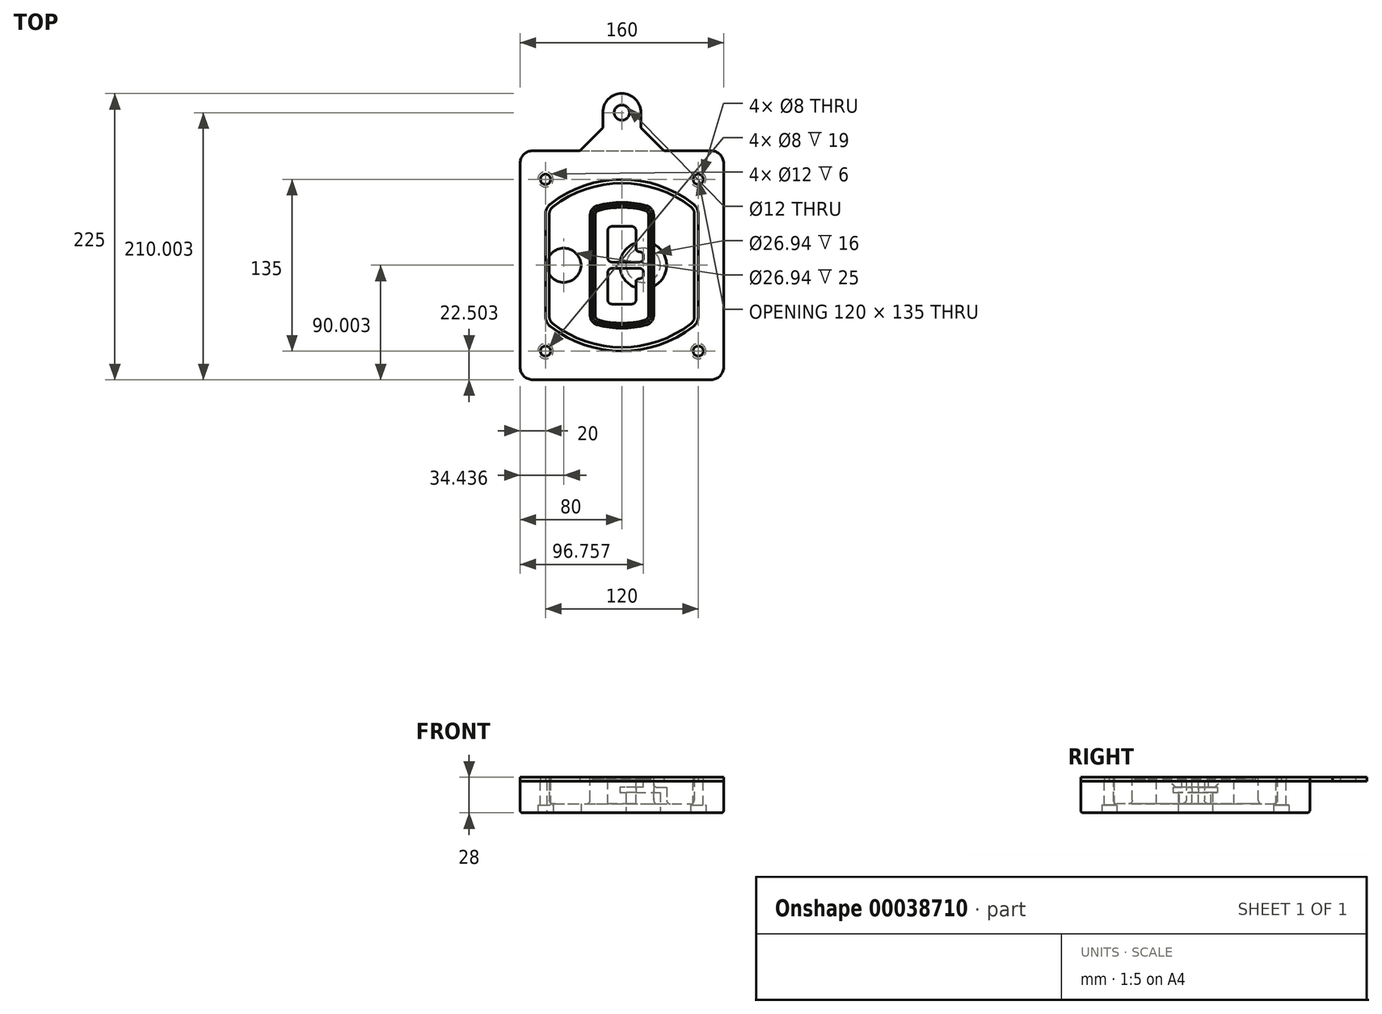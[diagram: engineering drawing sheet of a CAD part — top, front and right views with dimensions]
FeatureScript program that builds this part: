
annotation { "Feature Type Name" : "Feature", "Feature Type Description" : "" }
export const myFeature = defineFeature(function(context is Context, id is Id, definition is map)
    precondition{}
    {
        {
            var Q0;
            Q0=qCreatedBy(makeId("Top.planeOp"),FACE);
            var sketch = newSketch(context, id + "F0", { "sketchPlane" : qUnion([Q0])});
            skPoint(sketch, "E0.rect.middle", {"position": v(0, 0) * mm});
            skLineSegment(sketch, "E1.bottom", {"start": v(24.05, 28.38) * mm, "end": v(164.05, 28.38) * mm});
            skLineSegment(sketch, "E1.top", {"start": v(24.05, 208.38) * mm, "end": v(164.05, 208.38) * mm});
            skLineSegment(sketch, "E1.left", {"start": v(14.05, 38.38) * mm, "end": v(14.05, 198.38) * mm});
            skLineSegment(sketch, "E1.right", {"start": v(174.05, 38.38) * mm, "end": v(174.05, 198.38) * mm});
            skLineSegment(sketch, "E2", {"start": v(14.05, 208.38) * mm, "end": v(174.05, 28.38) * mm, "construction": true});
            skLineSegment(sketch, "E3", {"start": v(174.05, 208.38) * mm, "end": v(14.05, 28.38) * mm, "construction": true});
            skCircle(sketch, "E4", {"center": v(34.05, 185.88) * mm, "radius": 4 * mm});
            skCircle(sketch, "E5", {"center": v(154.05, 185.88) * mm, "radius": 4 * mm});
            skCircle(sketch, "E6", {"center": v(154.05, 50.88) * mm, "radius": 4 * mm});
            skCircle(sketch, "E7", {"center": v(34.05, 50.88) * mm, "radius": 4 * mm});
            skLineSegment(sketch, "E8", {"start": v(34.05, 185.88) * mm, "end": v(154.05, 185.88) * mm, "construction": true});
            skLineSegment(sketch, "E9", {"start": v(154.05, 185.88) * mm, "end": v(154.05, 50.88) * mm, "construction": true});
            skLineSegment(sketch, "E10", {"start": v(154.05, 50.88) * mm, "end": v(34.05, 50.88) * mm, "construction": true});
            skLineSegment(sketch, "E11", {"start": v(34.05, 50.88) * mm, "end": v(34.05, 185.88) * mm, "construction": true});
            skLineSegment(sketch, "E12", {"start": v(34.05, 158.68) * mm, "end": v(34.05, 78.09) * mm});
            skLineSegment(sketch, "E13", {"start": v(154.05, 158.68) * mm, "end": v(154.05, 78.09) * mm});
            skArc(sketch, "E14", {"start": v(150.2, 166.56) * mm, "mid": v(94.05, 185.88) * mm, "end": v(37.9, 166.56) * mm});
            skArc(sketch, "E15", {"start": v(37.9, 70.2) * mm, "mid": v(94.05, 50.88) * mm, "end": v(150.2, 70.2) * mm});
            skLineSegment(sketch, "E16", {"start": v(34.05, 118.38) * mm, "end": v(154.05, 118.38) * mm, "construction": true});
            skPoint(sketch, "E17.visualSharp", {"position": v(34.05, 73.38) * mm});
            skArc(sketch, "E17.filletArc", {"start": v(34.05, 78.09) * mm, "mid": v(35.06, 73.7) * mm, "end": v(37.9, 70.2) * mm});
            skPoint(sketch, "E18.visualSharp", {"position": v(34.05, 163.38) * mm});
            skArc(sketch, "E18.filletArc", {"start": v(37.9, 166.56) * mm, "mid": v(35.06, 163.06) * mm, "end": v(34.05, 158.68) * mm});
            skPoint(sketch, "E19.visualSharp", {"position": v(154.05, 163.38) * mm});
            skArc(sketch, "E19.filletArc", {"start": v(154.05, 158.68) * mm, "mid": v(153.04, 163.06) * mm, "end": v(150.2, 166.56) * mm});
            skPoint(sketch, "E20.visualSharp", {"position": v(154.05, 73.38) * mm});
            skArc(sketch, "E20.filletArc", {"start": v(150.2, 70.2) * mm, "mid": v(153.04, 73.7) * mm, "end": v(154.05, 78.09) * mm});
            skPoint(sketch, "E21.visualSharp", {"position": v(14.05, 208.38) * mm});
            skArc(sketch, "E21.filletArc", {"start": v(24.05, 208.38) * mm, "mid": v(16.98, 205.45) * mm, "end": v(14.05, 198.38) * mm});
            skPoint(sketch, "E22.visualSharp", {"position": v(174.05, 208.38) * mm});
            skArc(sketch, "E22.filletArc", {"start": v(174.05, 198.38) * mm, "mid": v(171.12, 205.45) * mm, "end": v(164.05, 208.38) * mm});
            skPoint(sketch, "E23.visualSharp", {"position": v(174.05, 28.38) * mm});
            skArc(sketch, "E23.filletArc", {"start": v(164.05, 28.38) * mm, "mid": v(171.12, 31.31) * mm, "end": v(174.05, 38.38) * mm});
            skPoint(sketch, "E24.visualSharp", {"position": v(14.05, 28.38) * mm});
            skArc(sketch, "E24.filletArc", {"start": v(14.05, 38.38) * mm, "mid": v(16.98, 31.31) * mm, "end": v(24.05, 28.38) * mm});
            skArc(sketch, "E25.0", {"start": v(151.05, 158.68) * mm, "mid": v(150.34, 161.75) * mm, "end": v(148.36, 164.2) * mm});
            skLineSegment(sketch, "E25.1", {"start": v(151.05, 158.68) * mm, "end": v(151.05, 78.09) * mm});
            skArc(sketch, "E25.2", {"start": v(148.36, 72.57) * mm, "mid": v(150.34, 75.02) * mm, "end": v(151.05, 78.09) * mm});
            skArc(sketch, "E25.3", {"start": v(39.74, 72.57) * mm, "mid": v(94.05, 53.88) * mm, "end": v(148.36, 72.57) * mm});
            skArc(sketch, "E25.4", {"start": v(37.05, 78.09) * mm, "mid": v(37.76, 75.02) * mm, "end": v(39.74, 72.57) * mm});
            skArc(sketch, "E25.5", {"start": v(148.36, 164.2) * mm, "mid": v(94.05, 182.88) * mm, "end": v(39.74, 164.2) * mm});
            skLineSegment(sketch, "E25.6", {"start": v(37.05, 158.68) * mm, "end": v(37.05, 78.09) * mm});
            skArc(sketch, "E25.7", {"start": v(39.74, 164.2) * mm, "mid": v(37.76, 161.75) * mm, "end": v(37.05, 158.68) * mm});
            skArc(sketch, "E26.0", {"start": v(35.43, 169.71) * mm, "mid": v(31.47, 164.82) * mm, "end": v(30.05, 158.68) * mm});
            skArc(sketch, "E26.1", {"start": v(152.67, 169.71) * mm, "mid": v(94.05, 189.88) * mm, "end": v(35.43, 169.71) * mm});
            skArc(sketch, "E26.2", {"start": v(158.05, 158.68) * mm, "mid": v(156.63, 164.82) * mm, "end": v(152.67, 169.71) * mm});
            skLineSegment(sketch, "E26.3", {"start": v(158.05, 158.68) * mm, "end": v(158.05, 78.09) * mm});
            skArc(sketch, "E26.4", {"start": v(152.67, 67.05) * mm, "mid": v(156.63, 71.95) * mm, "end": v(158.05, 78.09) * mm});
            skLineSegment(sketch, "E26.5", {"start": v(30.05, 158.68) * mm, "end": v(30.05, 78.09) * mm});
            skArc(sketch, "E26.6", {"start": v(35.43, 67.05) * mm, "mid": v(94.05, 46.88) * mm, "end": v(152.67, 67.05) * mm});
            skArc(sketch, "E26.7", {"start": v(30.05, 78.09) * mm, "mid": v(31.47, 71.95) * mm, "end": v(35.43, 67.05) * mm});
            skSolve(sketch);
        }
        {
            var Q0;
            Q0=makeQuery(id+"F0.imprint","IMPRINT",FACE,{"disambiguationData":[TD([[makeQuery(id+"F0.imprint","IMPRINT",EDGE,{"derivedFrom":sQuery(id+"F0.wireOp",EDGE,"E1.bottom")}),1.0]])]});
            var Q1;
            Q1=makeQuery(id+"F0.imprint","IMPRINT",FACE,{"disambiguationData":[TD([[makeQuery(id+"F0.imprint","IMPRINT",EDGE,{"derivedFrom":sQuery(id+"F0.wireOp",EDGE,"E12")}),1.0]])]});
            var Q2;
            Q2=makeQuery(id+"F0.imprint","IMPRINT",FACE,{"disambiguationData":[TD([[makeQuery(id+"F0.imprint","IMPRINT",EDGE,{"derivedFrom":sQuery(id+"F0.wireOp",EDGE,"E25.0")}),1.0]])]});
            var Q3;
            Q3=makeQuery(id+"F0.imprint","IMPRINT",FACE,{"disambiguationData":[TD([[makeQuery(id+"F0.imprint","IMPRINT",EDGE,{"derivedFrom":sQuery(id+"F0.wireOp",EDGE,"E12")}),-1.0]])]});
            extrude(context, id + "F1", {"entities" : qUnion([Q0, Q1, Q2, Q3]), "oppositeDirection" : true, "depth" : 25 * mm});
        }
        {
            var Q0;
            Q0=makeQuery(id+"F0.imprint","IMPRINT",FACE,{"disambiguationData":[TD([[makeQuery(id+"F0.imprint","IMPRINT",EDGE,{"derivedFrom":sQuery(id+"F0.wireOp",EDGE,"E12")}),1.0]])]});
            extrude(context, id + "F2", {"entities" : qUnion([Q0]), "operationType" : NewBodyOperationType.ADD, "depth" : 3 * mm});
        }
        {
            var Q0;
            Q0=makeQuery(id+"F0.imprint","IMPRINT",FACE,{"disambiguationData":[TD([[makeQuery(id+"F0.imprint","IMPRINT",EDGE,{"derivedFrom":sQuery(id+"F0.wireOp",EDGE,"E25.0")}),1.0]])]});
            extrude(context, id + "F3", {"entities" : qUnion([Q0]), "operationType" : NewBodyOperationType.REMOVE, "oppositeDirection" : true, "depth" : 18 * mm});
        }
        {
            var Q0;
            Q0=makeQuery(id+"F2.opExtrude","CAP_FACE",FACE,{"disambiguationData":[OSD([sQuery(id+"F0.wireOp",EDGE,"E12"),sQuery(id+"F0.wireOp",EDGE,"E13"),sQuery(id+"F0.wireOp",EDGE,"E14"),sQuery(id+"F0.wireOp",EDGE,"E15"),sQuery(id+"F0.wireOp",EDGE,"E17.filletArc"),sQuery(id+"F0.wireOp",EDGE,"E18.filletArc"),sQuery(id+"F0.wireOp",EDGE,"E19.filletArc"),sQuery(id+"F0.wireOp",EDGE,"E20.filletArc"),sQuery(id+"F0.wireOp",EDGE,"E25.0"),sQuery(id+"F0.wireOp",EDGE,"E25.1"),sQuery(id+"F0.wireOp",EDGE,"E25.2"),sQuery(id+"F0.wireOp",EDGE,"E25.3"),sQuery(id+"F0.wireOp",EDGE,"E25.4"),sQuery(id+"F0.wireOp",EDGE,"E25.5"),sQuery(id+"F0.wireOp",EDGE,"E25.6"),sQuery(id+"F0.wireOp",EDGE,"E25.7")])],"isStart":false});
            var sketch = newSketch(context, id + "F4", { "sketchPlane" : qUnion([Q0])});
            skArc(sketch, "E27.0", {"start": v(74.97, 71.41) * mm, "mid": v(94.05, 68.88) * mm, "end": v(113.13, 71.41) * mm});
            skArc(sketch, "E28.0", {"start": v(113.13, 165.35) * mm, "mid": v(94.05, 167.88) * mm, "end": v(74.97, 165.35) * mm});
            skLineSegment(sketch, "E29", {"start": v(69.05, 157.63) * mm, "end": v(69.05, 79.14) * mm});
            skLineSegment(sketch, "E30", {"start": v(119.05, 157.63) * mm, "end": v(119.05, 79.14) * mm});
            skLineSegment(sketch, "E31", {"start": v(69.05, 163.48) * mm, "end": v(119.05, 163.48) * mm, "construction": true});
            skLineSegment(sketch, "E32", {"start": v(69.05, 73.28) * mm, "end": v(119.05, 73.28) * mm, "construction": true});
            skPoint(sketch, "E33.visualSharp", {"position": v(69.05, 163.48) * mm});
            skArc(sketch, "E33.filletArc", {"start": v(74.97, 165.35) * mm, "mid": v(70.7, 162.5) * mm, "end": v(69.05, 157.63) * mm});
            skPoint(sketch, "E34.visualSharp", {"position": v(119.05, 163.48) * mm});
            skArc(sketch, "E34.filletArc", {"start": v(119.05, 157.63) * mm, "mid": v(117.4, 162.5) * mm, "end": v(113.13, 165.35) * mm});
            skPoint(sketch, "E35.visualSharp", {"position": v(119.05, 73.28) * mm});
            skArc(sketch, "E35.filletArc", {"start": v(113.13, 71.41) * mm, "mid": v(117.4, 74.27) * mm, "end": v(119.05, 79.14) * mm});
            skPoint(sketch, "E36.visualSharp", {"position": v(69.05, 73.28) * mm});
            skArc(sketch, "E36.filletArc", {"start": v(69.05, 79.14) * mm, "mid": v(70.7, 74.27) * mm, "end": v(74.97, 71.41) * mm});
            skArc(sketch, "E37.0", {"start": v(148.36, 164.2) * mm, "mid": v(94.05, 182.88) * mm, "end": v(39.74, 164.2) * mm});
            skArc(sketch, "E37.1", {"start": v(39.74, 164.2) * mm, "mid": v(37.76, 161.75) * mm, "end": v(37.05, 158.68) * mm});
            skLineSegment(sketch, "E37.2", {"start": v(37.05, 158.68) * mm, "end": v(37.05, 78.09) * mm});
            skArc(sketch, "E37.3", {"start": v(37.05, 78.09) * mm, "mid": v(37.76, 75.02) * mm, "end": v(39.74, 72.57) * mm});
            skArc(sketch, "E37.4", {"start": v(39.74, 72.57) * mm, "mid": v(94.05, 53.88) * mm, "end": v(148.36, 72.57) * mm});
            skArc(sketch, "E37.5", {"start": v(148.36, 72.57) * mm, "mid": v(150.34, 75.02) * mm, "end": v(151.05, 78.09) * mm});
            skLineSegment(sketch, "E37.6", {"start": v(151.05, 158.68) * mm, "end": v(151.05, 78.09) * mm});
            skArc(sketch, "E37.7", {"start": v(151.05, 158.68) * mm, "mid": v(150.34, 161.75) * mm, "end": v(148.36, 164.2) * mm});
            skLineSegment(sketch, "E38.0", {"start": v(117.05, 157.63) * mm, "end": v(117.05, 79.14) * mm});
            skArc(sketch, "E38.1", {"start": v(112.61, 73.34) * mm, "mid": v(115.81, 75.49) * mm, "end": v(117.05, 79.14) * mm});
            skArc(sketch, "E38.2", {"start": v(75.49, 73.34) * mm, "mid": v(94.05, 70.88) * mm, "end": v(112.61, 73.34) * mm});
            skArc(sketch, "E38.3", {"start": v(71.05, 79.14) * mm, "mid": v(72.29, 75.49) * mm, "end": v(75.49, 73.34) * mm});
            skLineSegment(sketch, "E38.4", {"start": v(71.05, 157.63) * mm, "end": v(71.05, 79.14) * mm});
            skArc(sketch, "E38.5", {"start": v(117.05, 157.63) * mm, "mid": v(115.81, 161.28) * mm, "end": v(112.61, 163.42) * mm});
            skArc(sketch, "E38.6", {"start": v(75.49, 163.42) * mm, "mid": v(72.29, 161.28) * mm, "end": v(71.05, 157.63) * mm});
            skArc(sketch, "E38.7", {"start": v(112.61, 163.42) * mm, "mid": v(94.05, 165.88) * mm, "end": v(75.49, 163.42) * mm});
            skArc(sketch, "E39.0", {"start": v(115.05, 157.63) * mm, "mid": v(114.23, 160.06) * mm, "end": v(112.1, 161.5) * mm});
            skLineSegment(sketch, "E39.1", {"start": v(115.05, 157.63) * mm, "end": v(115.05, 79.14) * mm});
            skArc(sketch, "E39.2", {"start": v(112.1, 75.27) * mm, "mid": v(114.23, 76.7) * mm, "end": v(115.05, 79.14) * mm});
            skArc(sketch, "E39.3", {"start": v(76, 75.27) * mm, "mid": v(94.05, 72.88) * mm, "end": v(112.1, 75.27) * mm});
            skArc(sketch, "E39.4", {"start": v(73.05, 79.14) * mm, "mid": v(73.87, 76.7) * mm, "end": v(76, 75.27) * mm});
            skArc(sketch, "E39.5", {"start": v(112.1, 161.5) * mm, "mid": v(94.05, 163.88) * mm, "end": v(76, 161.5) * mm});
            skLineSegment(sketch, "E39.6", {"start": v(73.05, 157.63) * mm, "end": v(73.05, 79.14) * mm});
            skArc(sketch, "E39.7", {"start": v(76, 161.5) * mm, "mid": v(73.87, 160.06) * mm, "end": v(73.05, 157.63) * mm});
            skLineSegment(sketch, "E40", {"start": v(69.05, 118.38) * mm, "end": v(119.05, 118.38) * mm, "construction": true});
            skLineSegment(sketch, "E41", {"start": v(83.05, 123.88) * mm, "end": v(83.05, 145.88) * mm});
            skLineSegment(sketch, "E42", {"start": v(86.05, 148.88) * mm, "end": v(102.05, 148.88) * mm});
            skLineSegment(sketch, "E43", {"start": v(105.05, 145.88) * mm, "end": v(105.05, 131.88) * mm});
            skLineSegment(sketch, "E44", {"start": v(108.05, 128.88) * mm, "end": v(108.05, 128.88) * mm});
            skLineSegment(sketch, "E45", {"start": v(111.05, 125.88) * mm, "end": v(111.05, 123.88) * mm});
            skLineSegment(sketch, "E46", {"start": v(108.05, 120.88) * mm, "end": v(86.05, 120.88) * mm});
            skPoint(sketch, "E47.visualSharp", {"position": v(83.05, 148.88) * mm});
            skArc(sketch, "E47.filletArc", {"start": v(86.05, 148.88) * mm, "mid": v(83.93, 148) * mm, "end": v(83.05, 145.88) * mm});
            skPoint(sketch, "E48.visualSharp", {"position": v(105.05, 148.88) * mm});
            skArc(sketch, "E48.filletArc", {"start": v(105.05, 145.88) * mm, "mid": v(104.17, 148) * mm, "end": v(102.05, 148.88) * mm});
            skPoint(sketch, "E49.visualSharp", {"position": v(105.05, 128.88) * mm});
            skArc(sketch, "E49.filletArc", {"start": v(105.05, 131.88) * mm, "mid": v(105.93, 129.76) * mm, "end": v(108.05, 128.88) * mm});
            skPoint(sketch, "E50.visualSharp", {"position": v(111.05, 128.88) * mm});
            skArc(sketch, "E50.filletArc", {"start": v(111.05, 125.88) * mm, "mid": v(110.17, 128) * mm, "end": v(108.05, 128.88) * mm});
            skPoint(sketch, "E51.visualSharp", {"position": v(111.05, 120.88) * mm});
            skArc(sketch, "E51.filletArc", {"start": v(108.05, 120.88) * mm, "mid": v(110.17, 121.76) * mm, "end": v(111.05, 123.88) * mm});
            skPoint(sketch, "E52.visualSharp", {"position": v(83.05, 120.88) * mm});
            skArc(sketch, "E52.filletArc", {"start": v(83.05, 123.88) * mm, "mid": v(83.93, 121.76) * mm, "end": v(86.05, 120.88) * mm});
            skLineSegment(sketch, "E53.0.MirrorCS", {"start": v(108.05, 115.88) * mm, "end": v(86.05, 115.88) * mm});
            skArc(sketch, "E54.0.MirrorCS", {"start": v(83.05, 112.88) * mm, "mid": v(83.93, 115) * mm, "end": v(86.05, 115.88) * mm});
            skLineSegment(sketch, "E55.0.MirrorCS", {"start": v(83.05, 112.88) * mm, "end": v(83.05, 90.88) * mm});
            skArc(sketch, "E56.0.MirrorCS", {"start": v(86.05, 87.88) * mm, "mid": v(83.93, 88.76) * mm, "end": v(83.05, 90.88) * mm});
            skLineSegment(sketch, "E57.0.MirrorCS", {"start": v(86.05, 87.88) * mm, "end": v(102.05, 87.88) * mm});
            skArc(sketch, "E58.0.MirrorCS", {"start": v(105.05, 90.88) * mm, "mid": v(104.17, 88.76) * mm, "end": v(102.05, 87.88) * mm});
            skLineSegment(sketch, "E59.0.MirrorCS", {"start": v(105.05, 90.88) * mm, "end": v(105.05, 104.88) * mm});
            skArc(sketch, "E60.0.MirrorCS", {"start": v(105.05, 104.88) * mm, "mid": v(105.93, 107) * mm, "end": v(108.05, 107.88) * mm});
            skArc(sketch, "E61.0.MirrorCS", {"start": v(111.05, 110.88) * mm, "mid": v(110.17, 108.76) * mm, "end": v(108.05, 107.88) * mm});
            skLineSegment(sketch, "E62.0.MirrorCS", {"start": v(111.05, 110.88) * mm, "end": v(111.05, 112.88) * mm});
            skArc(sketch, "E63.0.MirrorCS", {"start": v(108.05, 115.88) * mm, "mid": v(110.17, 115) * mm, "end": v(111.05, 112.88) * mm});
            skSolve(sketch);
        }
        {
            var Q0;
            Q0=makeQuery(id+"F4.imprint","IMPRINT",FACE,{"disambiguationData":[TD([[makeQuery(id+"F4.imprint","IMPRINT",EDGE,{"derivedFrom":sQuery(id+"F4.wireOp",EDGE,"E27.0")}),1.0]])]});
            var Q1;
            Q1=makeQuery(id+"F4.imprint","IMPRINT",FACE,{"disambiguationData":[TD([[makeQuery(id+"F4.imprint","IMPRINT",EDGE,{"derivedFrom":sQuery(id+"F4.wireOp",EDGE,"E38.0")}),-1.0]])]});
            var Q2;
            Q2=makeQuery(id+"F4.imprint","IMPRINT",FACE,{"disambiguationData":[TD([[makeQuery(id+"F4.imprint","IMPRINT",EDGE,{"derivedFrom":sQuery(id+"F4.wireOp",EDGE,"E39.0")}),1.0]])]});
            extrude(context, id + "F5", {"entities" : qUnion([Q0, Q1, Q2]), "operationType" : NewBodyOperationType.ADD, "endBound" : BoundingType.UP_TO_NEXT, "oppositeDirection" : true, "depth" : 25 * mm});
        }
        {
            var Q0;
            Q0=makeQuery(id+"F4.imprint","IMPRINT",FACE,{"disambiguationData":[TD([[makeQuery(id+"F4.imprint","IMPRINT",EDGE,{"derivedFrom":sQuery(id+"F4.wireOp",EDGE,"E38.0")}),-1.0]])]});
            extrude(context, id + "F6", {"entities" : qUnion([Q0]), "operationType" : NewBodyOperationType.REMOVE, "oppositeDirection" : true, "depth" : 2 * mm});
        }
        {
            var Q0;
            Q0=makeQuery(id+"F1.opExtrude","CAP_FACE",FACE,{"disambiguationData":[OSD([sQuery(id+"F0.wireOp",EDGE,"E1.bottom"),sQuery(id+"F0.wireOp",EDGE,"E1.top"),sQuery(id+"F0.wireOp",EDGE,"E1.left"),sQuery(id+"F0.wireOp",EDGE,"E1.right"),sQuery(id+"F0.wireOp",EDGE,"E4"),sQuery(id+"F0.wireOp",EDGE,"E5"),sQuery(id+"F0.wireOp",EDGE,"E6"),sQuery(id+"F0.wireOp",EDGE,"E7"),sQuery(id+"F0.wireOp",EDGE,"E21.filletArc"),sQuery(id+"F0.wireOp",EDGE,"E22.filletArc"),sQuery(id+"F0.wireOp",EDGE,"E23.filletArc"),sQuery(id+"F0.wireOp",EDGE,"E24.filletArc")])],"isStart":false});
            var sketch = newSketch(context, id + "F7", { "sketchPlane" : qUnion([Q0])});
            skCircle(sketch, "E64", {"center": v(110.8, -118.38) * mm, "radius": 13.47 * mm});
            skCircle(sketch, "E65", {"center": v(48.49, -118.38) * mm, "radius": 13.47 * mm});
            skLineSegment(sketch, "E66", {"start": v(174.05, -118.38) * mm, "end": v(14.05, -118.38) * mm});
            skCircle(sketch, "E67", {"center": v(110.8, -118.38) * mm, "radius": 18.47 * mm});
            skCircle(sketch, "E68", {"center": v(154.05, -185.88) * mm, "radius": 6 * mm});
            skCircle(sketch, "E69", {"center": v(34.05, -185.88) * mm, "radius": 6 * mm});
            skCircle(sketch, "E70", {"center": v(34.05, -50.88) * mm, "radius": 6 * mm});
            skCircle(sketch, "E71", {"center": v(154.05, -50.88) * mm, "radius": 6 * mm});
            skSolve(sketch);
        }
        {
            var Q0;
            {var subQ1=sQuery(id+"F7.wireOp",EDGE,"E66");var subQ4=sQuery(id+"F7.wireOp",EDGE,"E64");var subQ6=makeQuery(id+"F7.imprint","INTERSECT",VERTEX,{"disambiguationData":[OD(0.0)],"derivedFrom":[subQ4,subQ1]});Q0=makeQuery(id+"F7.imprint","IMPRINT",FACE,{"disambiguationData":[TD([[makeQuery(id+"F7.imprint","IMPRINT",EDGE,{"disambiguationData":[TD([[subQ6,-1.0]])],"derivedFrom":subQ4}),-1.0]])]});}
            var Q1;
            {var subQ0=sQuery(id+"F7.wireOp",EDGE,"E66");var subQ1=sQuery(id+"F7.wireOp",EDGE,"E64");var subQ3=makeQuery(id+"F7.imprint","INTERSECT",VERTEX,{"disambiguationData":[OD(0.0)],"derivedFrom":[subQ1,subQ0]});Q1=makeQuery(id+"F7.imprint","IMPRINT",FACE,{"disambiguationData":[TD([[makeQuery(id+"F7.imprint","IMPRINT",EDGE,{"disambiguationData":[TD([[subQ3,-1.0]])],"derivedFrom":subQ1}),1.0]])]});}
            var Q2;
            {var subQ0=sQuery(id+"F7.wireOp",EDGE,"E66");var subQ1=sQuery(id+"F7.wireOp",EDGE,"E64");var subQ3=makeQuery(id+"F7.imprint","INTERSECT",VERTEX,{"disambiguationData":[OD(0.0)],"derivedFrom":[subQ1,subQ0]});Q2=makeQuery(id+"F7.imprint","IMPRINT",FACE,{"disambiguationData":[TD([[makeQuery(id+"F7.imprint","IMPRINT",EDGE,{"disambiguationData":[TD([[subQ3,1.0]])],"derivedFrom":subQ1}),1.0]])]});}
            var Q3;
            {var subQ1=sQuery(id+"F7.wireOp",EDGE,"E66");var subQ4=sQuery(id+"F7.wireOp",EDGE,"E64");var subQ6=makeQuery(id+"F7.imprint","INTERSECT",VERTEX,{"disambiguationData":[OD(0.0)],"derivedFrom":[subQ4,subQ1]});Q3=makeQuery(id+"F7.imprint","IMPRINT",FACE,{"disambiguationData":[TD([[makeQuery(id+"F7.imprint","IMPRINT",EDGE,{"disambiguationData":[TD([[subQ6,1.0]])],"derivedFrom":subQ4}),-1.0]])]});}
            extrude(context, id + "F8", {"entities" : qUnion([Q0, Q1, Q2, Q3]), "operationType" : NewBodyOperationType.ADD, "oppositeDirection" : true, "depth" : 20 * mm});
        }
        {
            var Q0;
            {var subQ0=sQuery(id+"F7.wireOp",EDGE,"E66");var subQ1=sQuery(id+"F7.wireOp",EDGE,"E64");var subQ3=makeQuery(id+"F7.imprint","INTERSECT",VERTEX,{"disambiguationData":[OD(0.0)],"derivedFrom":[subQ1,subQ0]});Q0=makeQuery(id+"F7.imprint","IMPRINT",FACE,{"disambiguationData":[TD([[makeQuery(id+"F7.imprint","IMPRINT",EDGE,{"disambiguationData":[TD([[subQ3,-1.0]])],"derivedFrom":subQ1}),1.0]])]});}
            var Q1;
            {var subQ0=sQuery(id+"F7.wireOp",EDGE,"E66");var subQ1=sQuery(id+"F7.wireOp",EDGE,"E64");var subQ3=makeQuery(id+"F7.imprint","INTERSECT",VERTEX,{"disambiguationData":[OD(0.0)],"derivedFrom":[subQ1,subQ0]});Q1=makeQuery(id+"F7.imprint","IMPRINT",FACE,{"disambiguationData":[TD([[makeQuery(id+"F7.imprint","IMPRINT",EDGE,{"disambiguationData":[TD([[subQ3,1.0]])],"derivedFrom":subQ1}),1.0]])]});}
            extrude(context, id + "F9", {"entities" : qUnion([Q0, Q1]), "operationType" : NewBodyOperationType.REMOVE, "oppositeDirection" : true, "depth" : 16 * mm});
        }
        {
            var Q0;
            {var subQ0=sQuery(id+"F7.wireOp",EDGE,"E66");var subQ1=sQuery(id+"F7.wireOp",EDGE,"E65");var subQ3=makeQuery(id+"F7.imprint","INTERSECT",VERTEX,{"disambiguationData":[OD(0.0)],"derivedFrom":[subQ1,subQ0]});Q0=makeQuery(id+"F7.imprint","IMPRINT",FACE,{"disambiguationData":[TD([[makeQuery(id+"F7.imprint","IMPRINT",EDGE,{"disambiguationData":[TD([[subQ3,-1.0]])],"derivedFrom":subQ1}),1.0]])]});}
            var Q1;
            {var subQ0=sQuery(id+"F7.wireOp",EDGE,"E66");var subQ1=sQuery(id+"F7.wireOp",EDGE,"E65");var subQ3=makeQuery(id+"F7.imprint","INTERSECT",VERTEX,{"disambiguationData":[OD(0.0)],"derivedFrom":[subQ1,subQ0]});Q1=makeQuery(id+"F7.imprint","IMPRINT",FACE,{"disambiguationData":[TD([[makeQuery(id+"F7.imprint","IMPRINT",EDGE,{"disambiguationData":[TD([[subQ3,1.0]])],"derivedFrom":subQ1}),1.0]])]});}
            extrude(context, id + "F10", {"entities" : qUnion([Q0, Q1]), "operationType" : NewBodyOperationType.REMOVE, "oppositeDirection" : true, "depth" : 25 * mm});
        }
        {
            var Q0;
            Q0=makeQuery(id+"F7.imprint","IMPRINT",FACE,{"disambiguationData":[TD([[makeQuery(id+"F7.imprint","IMPRINT",EDGE,{"derivedFrom":sQuery(id+"F7.wireOp",EDGE,"E68")}),1.0]])]});
            var Q1;
            Q1=makeQuery(id+"F7.imprint","IMPRINT",FACE,{"disambiguationData":[TD([[makeQuery(id+"F7.imprint","IMPRINT",EDGE,{"derivedFrom":makeQuery(id+"F1.opExtrude","CAP_EDGE",EDGE,{"disambiguationData":[OSD([sQuery(id+"F0.wireOp",EDGE,"E5")])],"isStart":false})}),-1.0]])]});
            var Q2;
            Q2=makeQuery(id+"F7.imprint","IMPRINT",FACE,{"disambiguationData":[TD([[makeQuery(id+"F7.imprint","IMPRINT",EDGE,{"derivedFrom":sQuery(id+"F7.wireOp",EDGE,"E69")}),1.0]])]});
            var Q3;
            Q3=makeQuery(id+"F7.imprint","IMPRINT",FACE,{"disambiguationData":[TD([[makeQuery(id+"F7.imprint","IMPRINT",EDGE,{"derivedFrom":makeQuery(id+"F1.opExtrude","CAP_EDGE",EDGE,{"disambiguationData":[OSD([sQuery(id+"F0.wireOp",EDGE,"E4")])],"isStart":false})}),-1.0]])]});
            var Q4;
            Q4=makeQuery(id+"F7.imprint","IMPRINT",FACE,{"disambiguationData":[TD([[makeQuery(id+"F7.imprint","IMPRINT",EDGE,{"derivedFrom":sQuery(id+"F7.wireOp",EDGE,"E70")}),1.0]])]});
            var Q5;
            Q5=makeQuery(id+"F7.imprint","IMPRINT",FACE,{"disambiguationData":[TD([[makeQuery(id+"F7.imprint","IMPRINT",EDGE,{"derivedFrom":makeQuery(id+"F1.opExtrude","CAP_EDGE",EDGE,{"disambiguationData":[OSD([sQuery(id+"F0.wireOp",EDGE,"E7")])],"isStart":false})}),-1.0]])]});
            var Q6;
            Q6=makeQuery(id+"F7.imprint","IMPRINT",FACE,{"disambiguationData":[TD([[makeQuery(id+"F7.imprint","IMPRINT",EDGE,{"derivedFrom":sQuery(id+"F7.wireOp",EDGE,"E71")}),1.0]])]});
            var Q7;
            Q7=makeQuery(id+"F7.imprint","IMPRINT",FACE,{"disambiguationData":[TD([[makeQuery(id+"F7.imprint","IMPRINT",EDGE,{"derivedFrom":makeQuery(id+"F1.opExtrude","CAP_EDGE",EDGE,{"disambiguationData":[OSD([sQuery(id+"F0.wireOp",EDGE,"E6")])],"isStart":false})}),-1.0]])]});
            extrude(context, id + "F11", {"entities" : qUnion([Q0, Q1, Q2, Q3, Q4, Q5, Q6, Q7]), "operationType" : NewBodyOperationType.REMOVE, "oppositeDirection" : true, "depth" : 6 * mm});
        }
        {
            var Q0;
            Q0=makeQuery(id+"F9.boolean.opBoolean","COPY",FACE,{"derivedFrom":makeQuery(id+"F9.opExtrude","CAP_FACE",FACE,{"disambiguationData":[OSD([sQuery(id+"F7.wireOp",EDGE,"E64")])],"isStart":false})});
            var sketch = newSketch(context, id + "F12", { "sketchPlane" : qUnion([Q0])});
            skArc(sketch, "E72.0", {"start": v(105.05, -100.83) * mm, "mid": v(96.62, -106.56) * mm, "end": v(92.5, -115.88) * mm});
            skArc(sketch, "E72.1", {"start": v(92.5, -120.88) * mm, "mid": v(96.62, -130.2) * mm, "end": v(105.05, -135.93) * mm});
            skLineSegment(sketch, "E73", {"start": v(92.5, -120.88) * mm, "end": v(108.05, -120.88) * mm});
            skLineSegment(sketch, "E74.0", {"start": v(108.05, -115.88) * mm, "end": v(92.5, -115.88) * mm});
            skArc(sketch, "E74.1", {"start": v(108.05, -115.88) * mm, "mid": v(110.17, -115) * mm, "end": v(111.05, -112.88) * mm});
            skLineSegment(sketch, "E74.2", {"start": v(111.05, -110.88) * mm, "end": v(111.05, -112.88) * mm});
            skArc(sketch, "E74.3", {"start": v(111.05, -110.88) * mm, "mid": v(110.17, -108.76) * mm, "end": v(108.05, -107.88) * mm});
            skArc(sketch, "E74.4", {"start": v(105.05, -104.88) * mm, "mid": v(105.93, -107) * mm, "end": v(108.05, -107.88) * mm});
            skLineSegment(sketch, "E74.5", {"start": v(105.05, -100.83) * mm, "end": v(105.05, -104.88) * mm});
            skLineSegment(sketch, "E74.7", {"start": v(108.05, -120.88) * mm, "end": v(92.5, -120.88) * mm});
            skArc(sketch, "E74.8", {"start": v(108.05, -120.88) * mm, "mid": v(110.17, -121.76) * mm, "end": v(111.05, -123.88) * mm});
            skLineSegment(sketch, "E74.9", {"start": v(111.05, -125.88) * mm, "end": v(111.05, -123.88) * mm});
            skArc(sketch, "E74.10", {"start": v(111.05, -125.88) * mm, "mid": v(110.17, -128) * mm, "end": v(108.05, -128.88) * mm});
            skArc(sketch, "E74.11", {"start": v(105.05, -131.88) * mm, "mid": v(105.93, -129.76) * mm, "end": v(108.05, -128.88) * mm});
            skLineSegment(sketch, "E74.12", {"start": v(105.05, -135.93) * mm, "end": v(105.05, -131.88) * mm});
            skPoint(sketch, "E75.orphan", {"position": v(105.05, -145.88) * mm});
            skPoint(sketch, "E76.orphan", {"position": v(86.05, -120.88) * mm});
            skPoint(sketch, "E77.orphan", {"position": v(86.05, -115.88) * mm});
            skPoint(sketch, "E78.orphan", {"position": v(105.05, -90.88) * mm});
            skSolve(sketch);
        }
        {
            var Q0;
            {var subQ7=sQuery(id+"F12.wireOp",EDGE,"E72.0");var subQ14=sQuery(id+"F12.wireOp",EDGE,"E72.1");var subQ16=sQuery(id+"F12.wireOp",EDGE,"E74.1");var subQ18=sQuery(id+"F12.wireOp",EDGE,"E74.8");Q0=qUnion([makeQuery(id+"F12.imprint","IMPRINT",FACE,{"disambiguationData":[TD([[makeQuery(id+"F12.imprint","IMPRINT",EDGE,{"derivedFrom":subQ7}),1.0]])]}),makeQuery(id+"F12.imprint","IMPRINT",FACE,{"disambiguationData":[TD([[makeQuery(id+"F12.imprint","IMPRINT",EDGE,{"derivedFrom":subQ14}),1.0]])]}),makeQuery(id+"F12.imprint","IMPRINT",FACE,{"disambiguationData":[TD([[makeQuery(id+"F12.imprint","IMPRINT",EDGE,{"derivedFrom":subQ16}),1.0]])]}),makeQuery(id+"F12.imprint","IMPRINT",FACE,{"disambiguationData":[TD([[makeQuery(id+"F12.imprint","IMPRINT",EDGE,{"derivedFrom":subQ18}),-1.0]])]})]);}
            var Q1;
            Q1=makeQuery(id+"F5.boolean.opBoolean","SPLIT",FACE,{"disambiguationData":[TD([makeQuery(id+"F5.opExtrude","SWEPT_FACE",FACE,{"disambiguationData":[OSD([sQuery(id+"F4.wireOp",EDGE,"E41")])]})])],"derivedFrom":makeQuery(id+"F3.boolean.opBoolean","COPY",FACE,{"derivedFrom":makeQuery(id+"F3.opExtrude","CAP_FACE",FACE,{"disambiguationData":[OSD([sQuery(id+"F0.wireOp",EDGE,"E25.0"),sQuery(id+"F0.wireOp",EDGE,"E25.1"),sQuery(id+"F0.wireOp",EDGE,"E25.2"),sQuery(id+"F0.wireOp",EDGE,"E25.3"),sQuery(id+"F0.wireOp",EDGE,"E25.4"),sQuery(id+"F0.wireOp",EDGE,"E25.5"),sQuery(id+"F0.wireOp",EDGE,"E25.6"),sQuery(id+"F0.wireOp",EDGE,"E25.7")])],"isStart":false})})});
            extrude(context, id + "F13", {"entities" : qUnion([Q0]), "operationType" : NewBodyOperationType.REMOVE, "endBound" : BoundingType.UP_TO_SURFACE, "endBoundEntityFace" : qUnion([Q1]), "depth" : 25 * mm});
        }
        {
            var Q0;
            Q0=makeQuery(id+"F3.boolean.opBoolean","COPY",EDGE,{"derivedFrom":makeQuery(id+"F3.opExtrude","CAP_EDGE",EDGE,{"disambiguationData":[OSD([sQuery(id+"F0.wireOp",EDGE,"E25.6")])],"isStart":false})});
            var Q1;
            Q1=makeQuery(id+"F8.boolean.opBoolean","INTERSECT",EDGE,{"derivedFrom":[makeQuery(id+"F5.opExtrude","SWEPT_FACE",FACE,{"disambiguationData":[OSD([sQuery(id+"F4.wireOp",EDGE,"E30")])]}),makeQuery(id+"F8.opExtrude","CAP_FACE",FACE,{"disambiguationData":[OSD([sQuery(id+"F7.wireOp",EDGE,"E67")])],"isStart":false})]});
            var Q2;
            Q2=makeQuery(id+"F8.boolean.opBoolean","INTERSECT",EDGE,{"disambiguationData":[OD(1.0)],"derivedFrom":[makeQuery(id+"F5.opExtrude","SWEPT_FACE",FACE,{"disambiguationData":[OSD([sQuery(id+"F4.wireOp",EDGE,"E30")])]}),makeQuery(id+"F8.opExtrude","SWEPT_FACE",FACE,{"disambiguationData":[OSD([sQuery(id+"F7.wireOp",EDGE,"E67")])]})]});
            var Q3;
            {var subQ0=sQuery(id+"F4.wireOp",EDGE,"E30");Q3=makeQuery(id+"F8.boolean.opBoolean","SPLIT",EDGE,{"disambiguationData":[TD([makeQuery(id+"F5.opExtrude","SWEPT_FACE",FACE,{"disambiguationData":[OSD([sQuery(id+"F4.wireOp",EDGE,"E35.filletArc")])]})])],"derivedFrom":makeQuery(id+"F5.opExtrude","CAP_EDGE",EDGE,{"disambiguationData":[OSD([subQ0])],"isStart":false})});}
            var Q4;
            {var subQ0=sQuery(id+"F0.wireOp",EDGE,"E25.7");var subQ1=sQuery(id+"F0.wireOp",EDGE,"E25.1");var subQ2=sQuery(id+"F0.wireOp",EDGE,"E25.6");var subQ3=sQuery(id+"F0.wireOp",EDGE,"E25.5");var subQ4=sQuery(id+"F0.wireOp",EDGE,"E25.4");var subQ5=sQuery(id+"F0.wireOp",EDGE,"E25.0");var subQ6=sQuery(id+"F0.wireOp",EDGE,"E25.2");var subQ7=sQuery(id+"F0.wireOp",EDGE,"E25.3");Q4=makeQuery(id+"F8.boolean.opBoolean","INTERSECT",EDGE,{"derivedFrom":[makeQuery(id+"F5.boolean.opBoolean","SPLIT",FACE,{"disambiguationData":[TD([makeQuery(id+"F2.opExtrude","SWEPT_FACE",FACE,{"disambiguationData":[OSD([subQ5])]})])],"derivedFrom":makeQuery(id+"F3.boolean.opBoolean","COPY",FACE,{"derivedFrom":makeQuery(id+"F3.opExtrude","CAP_FACE",FACE,{"disambiguationData":[OSD([subQ5,subQ1,subQ6,subQ7,subQ4,subQ3,subQ2,subQ0])],"isStart":false})})}),makeQuery(id+"F8.opExtrude","SWEPT_FACE",FACE,{"disambiguationData":[OSD([sQuery(id+"F7.wireOp",EDGE,"E67")])]})]});}
            var Q5;
            Q5=makeQuery(id+"F8.boolean.opBoolean","INTERSECT",EDGE,{"disambiguationData":[OD(0.0)],"derivedFrom":[makeQuery(id+"F5.opExtrude","SWEPT_FACE",FACE,{"disambiguationData":[OSD([sQuery(id+"F4.wireOp",EDGE,"E30")])]}),makeQuery(id+"F8.opExtrude","SWEPT_FACE",FACE,{"disambiguationData":[OSD([sQuery(id+"F7.wireOp",EDGE,"E67")])]})]});
            fillet(context, id + "F14", {"entities" : qUnion([Q0, Q1, Q2, Q3, Q4, Q5]), "radius" : 3 * mm, "tangentPropagation" : true, "allowEdgeOverflow" : false});
        }
        {
            var Q0;
            Q0=makeQuery(id+"F1.opExtrude","CAP_EDGE",EDGE,{"disambiguationData":[OSD([sQuery(id+"F0.wireOp",EDGE,"E1.bottom")])],"isStart":false});
            fillet(context, id + "F15", {"entities" : qUnion([Q0]), "radius" : 2 * mm, "tangentPropagation" : true, "allowEdgeOverflow" : false});
        }
        {
            var Q0;
            {var subQ0=sQuery(id+"F0.wireOp",EDGE,"E1.bottom");var subQ1=sQuery(id+"F0.wireOp",EDGE,"E1.top");var subQ2=sQuery(id+"F0.wireOp",EDGE,"E1.left");var subQ3=sQuery(id+"F0.wireOp",EDGE,"E1.right");var subQ4=sQuery(id+"F0.wireOp",EDGE,"E4");var subQ5=sQuery(id+"F0.wireOp",EDGE,"E5");var subQ6=sQuery(id+"F0.wireOp",EDGE,"E6");var subQ7=sQuery(id+"F0.wireOp",EDGE,"E7");var subQ8=sQuery(id+"F0.wireOp",EDGE,"E21.filletArc");var subQ9=sQuery(id+"F0.wireOp",EDGE,"E22.filletArc");var subQ10=sQuery(id+"F0.wireOp",EDGE,"E23.filletArc");var subQ11=sQuery(id+"F0.wireOp",EDGE,"E24.filletArc");Q0=makeQuery(id+"F2.boolean.opBoolean","SPLIT",FACE,{"disambiguationData":[TD([makeQuery(id+"F1.opExtrude","SWEPT_FACE",FACE,{"disambiguationData":[OSD([subQ0])]})])],"derivedFrom":makeQuery(id+"F1.opExtrude","CAP_FACE",FACE,{"disambiguationData":[OSD([subQ0,subQ1,subQ2,subQ3,subQ4,subQ5,subQ6,subQ7,subQ8,subQ9,subQ10,subQ11])],"isStart":true})});}
            var sketch = newSketch(context, id + "F16", { "sketchPlane" : qUnion([Q0])});
            skLineSegment(sketch, "E79", {"start": v(94.05, 208.38) * mm, "end": v(94.05, 238.38) * mm, "construction": true});
            skCircle(sketch, "E80", {"center": v(94.05, 238.38) * mm, "radius": 6 * mm});
            skArc(sketch, "E81", {"start": v(79.05, 238.38) * mm, "mid": v(94.05, 253.38) * mm, "end": v(109.05, 238.38) * mm});
            skLineSegment(sketch, "E82", {"start": v(109.05, 238.38) * mm, "end": v(109.05, 226.38) * mm});
            skLineSegment(sketch, "E83", {"start": v(109.05, 226.38) * mm, "end": v(127.05, 208.38) * mm});
            skLineSegment(sketch, "E84.MirrorCS", {"start": v(79.05, 238.38) * mm, "end": v(79.05, 226.38) * mm});
            skLineSegment(sketch, "E85.MirrorCS", {"start": v(79.05, 226.38) * mm, "end": v(61.05, 208.38) * mm});
            skLineSegment(sketch, "E86", {"start": v(174.05, 118.38) * mm, "end": v(14.05, 118.38) * mm, "construction": true});
            skArc(sketch, "E87.MirrorCS", {"start": v(109.05, 238.38) * mm, "mid": v(94.05, 253.38) * mm, "end": v(79.05, 238.38) * mm});
            skArc(sketch, "E88.MirrorCS", {"start": v(79.05, -1.62) * mm, "mid": v(94.05, -16.62) * mm, "end": v(109.05, -1.62) * mm});
            skLineSegment(sketch, "E89.MirrorCS", {"start": v(109.05, -1.62) * mm, "end": v(109.05, 10.38) * mm});
            skLineSegment(sketch, "E90.MirrorCS", {"start": v(79.05, -1.62) * mm, "end": v(79.05, 10.38) * mm});
            skCircle(sketch, "E91.MirrorC", {"center": v(94.05, -1.62) * mm, "radius": 6 * mm});
            skLineSegment(sketch, "E92.MirrorCS", {"start": v(109.05, 10.38) * mm, "end": v(127.05, 28.38) * mm});
            skLineSegment(sketch, "E93.MirrorCS", {"start": v(79.05, 10.38) * mm, "end": v(61.05, 28.38) * mm});
            skArc(sketch, "E94.MirrorCS", {"start": v(109.05, -1.62) * mm, "mid": v(94.05, -16.62) * mm, "end": v(79.05, -1.62) * mm});
            skLineSegment(sketch, "E95.MirrorCS", {"start": v(94.05, 28.38) * mm, "end": v(94.05, -1.62) * mm});
            skSolve(sketch);
        }
        {
            var Q0;
            Q0=makeQuery(id+"F16.imprint","IMPRINT",FACE,{"disambiguationData":[TD([[makeQuery(id+"F16.imprint","IMPRINT",EDGE,{"derivedFrom":sQuery(id+"F16.wireOp",EDGE,"E94.MirrorCS")}),-1.0]])]});
            var Q1;
            {var subQ2=sQuery(id+"F16.wireOp",EDGE,"E85.MirrorCS");Q1=makeQuery(id+"F16.imprint","IMPRINT",FACE,{"disambiguationData":[TD([[makeQuery(id+"F16.imprint","IMPRINT",EDGE,{"derivedFrom":subQ2}),1.0]])]});}
            var Q2;
            Q2=makeQuery(id+"F16.imprint","IMPRINT",FACE,{"disambiguationData":[TD([[makeQuery(id+"F16.imprint","IMPRINT",EDGE,{"derivedFrom":makeQuery(id+"F1.opExtrude","CAP_EDGE",EDGE,{"disambiguationData":[OSD([sQuery(id+"F0.wireOp",EDGE,"E1.left")])],"isStart":true})}),-1.0]])]});
            var Q3;
            Q3=makeQuery(id+"F2.opExtrude","CAP_FACE",FACE,{"disambiguationData":[OSD([sQuery(id+"F0.wireOp",EDGE,"E12"),sQuery(id+"F0.wireOp",EDGE,"E13"),sQuery(id+"F0.wireOp",EDGE,"E14"),sQuery(id+"F0.wireOp",EDGE,"E15"),sQuery(id+"F0.wireOp",EDGE,"E17.filletArc"),sQuery(id+"F0.wireOp",EDGE,"E18.filletArc"),sQuery(id+"F0.wireOp",EDGE,"E19.filletArc"),sQuery(id+"F0.wireOp",EDGE,"E20.filletArc"),sQuery(id+"F0.wireOp",EDGE,"E25.0"),sQuery(id+"F0.wireOp",EDGE,"E25.1"),sQuery(id+"F0.wireOp",EDGE,"E25.2"),sQuery(id+"F0.wireOp",EDGE,"E25.3"),sQuery(id+"F0.wireOp",EDGE,"E25.4"),sQuery(id+"F0.wireOp",EDGE,"E25.5"),sQuery(id+"F0.wireOp",EDGE,"E25.6"),sQuery(id+"F0.wireOp",EDGE,"E25.7")])],"isStart":false});
            extrude(context, id + "F17", {"entities" : qUnion([Q0, Q1, Q2]), "endBound" : BoundingType.UP_TO_SURFACE, "endBoundEntityFace" : qUnion([Q3]), "depth" : 25 * mm});
        }
    });
